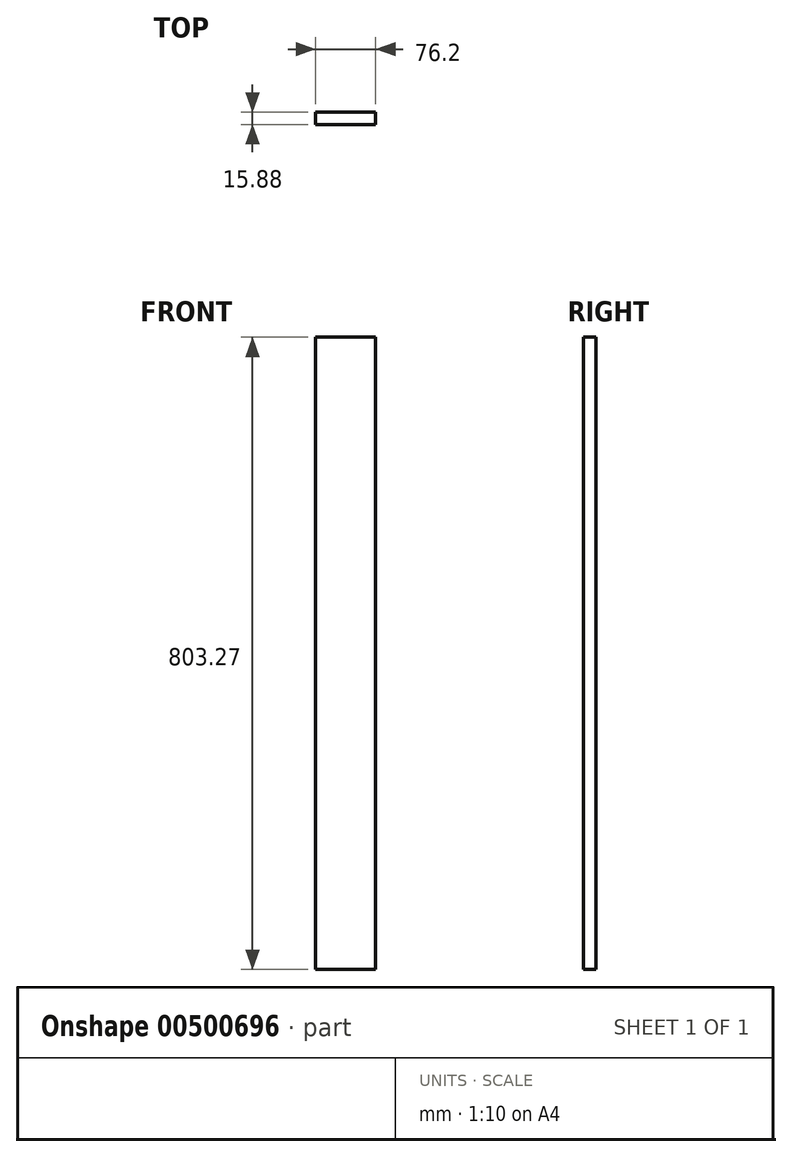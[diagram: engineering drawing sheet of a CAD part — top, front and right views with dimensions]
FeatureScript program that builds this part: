
annotation { "Feature Type Name" : "Feature", "Feature Type Description" : "" }
export const myFeature = defineFeature(function(context is Context, id is Id, definition is map)
    precondition{}
    {
        {
            var Q0;
            Q0=qCreatedBy(makeId("Front.planeOp"),FACE);
            var sketch = newSketch(context, id + "F0", { "sketchPlane" : qUnion([Q0])});
            skLineSegment(sketch, "E0.bottom", {"start": v(0, 0) * mm, "end": v(76.2, 0) * mm});
            skLineSegment(sketch, "E0.top", {"start": v(0, 803.28) * mm, "end": v(76.2, 803.28) * mm});
            skLineSegment(sketch, "E0.left", {"start": v(0, 0) * mm, "end": v(0, 803.27) * mm});
            skLineSegment(sketch, "E0.right", {"start": v(76.2, 0) * mm, "end": v(76.2, 803.27) * mm});
            skSolve(sketch);
        }
        {
            var Q0;
            Q0=makeQuery(id+"F0.imprint","IMPRINT",FACE,{"disambiguationData":[TD([[makeQuery(id+"F0.imprint","IMPRINT",EDGE,{"derivedFrom":sQuery(id+"F0.wireOp",EDGE,"E0.bottom")}),1.0]])]});
            extrude(context, id + "F1", {"entities" : qUnion([Q0]), "oppositeDirection" : true, "depth" : 15.88 * mm, "offsetDistance" : 25.4 * mm});
        }
    });
